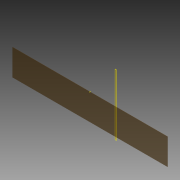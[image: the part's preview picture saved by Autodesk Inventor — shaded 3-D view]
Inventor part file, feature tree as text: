
AUTODESK INVENTOR PART (.ipt)
format: ipt  version: 2013 (Build 170138000, 138)  size: 88,576 bytes
history: native  units: in
note: dims shown in document units (in); Inventor stores cm internally (conversion verified against a paired STEP export)
features: reference x9, plane x2, extrude x1, sketch x1
ambient origin geometry x8: Origin, YZ Plane, XZ Plane, XY Plane, X Axis, Y Axis, Z Axis, Center Point
bodies: Solid1 (feature_tree)
feature tree (13):
  plane  "Work Plane1"
  extrude  "Extrusion1"  [1 undecoded]
  plane  "Work Plane2"
  sketch  "Sketch1"  dims[d0=0.25in d1=0.0in]
  reference  "Reference1"
  reference  "Reference2"
  reference  "Reference3"
  reference  "Reference4"
  reference  "Reference5"
  reference  "Reference6"
  reference  "Reference7"
  reference  "Reference8"
  reference  "Reference9"
note: 1 required parameter value undecoded (feature->parameter linkage not recoverable at this tier; creation-order binding heuristic only, values carry confidence <= 0.55)
